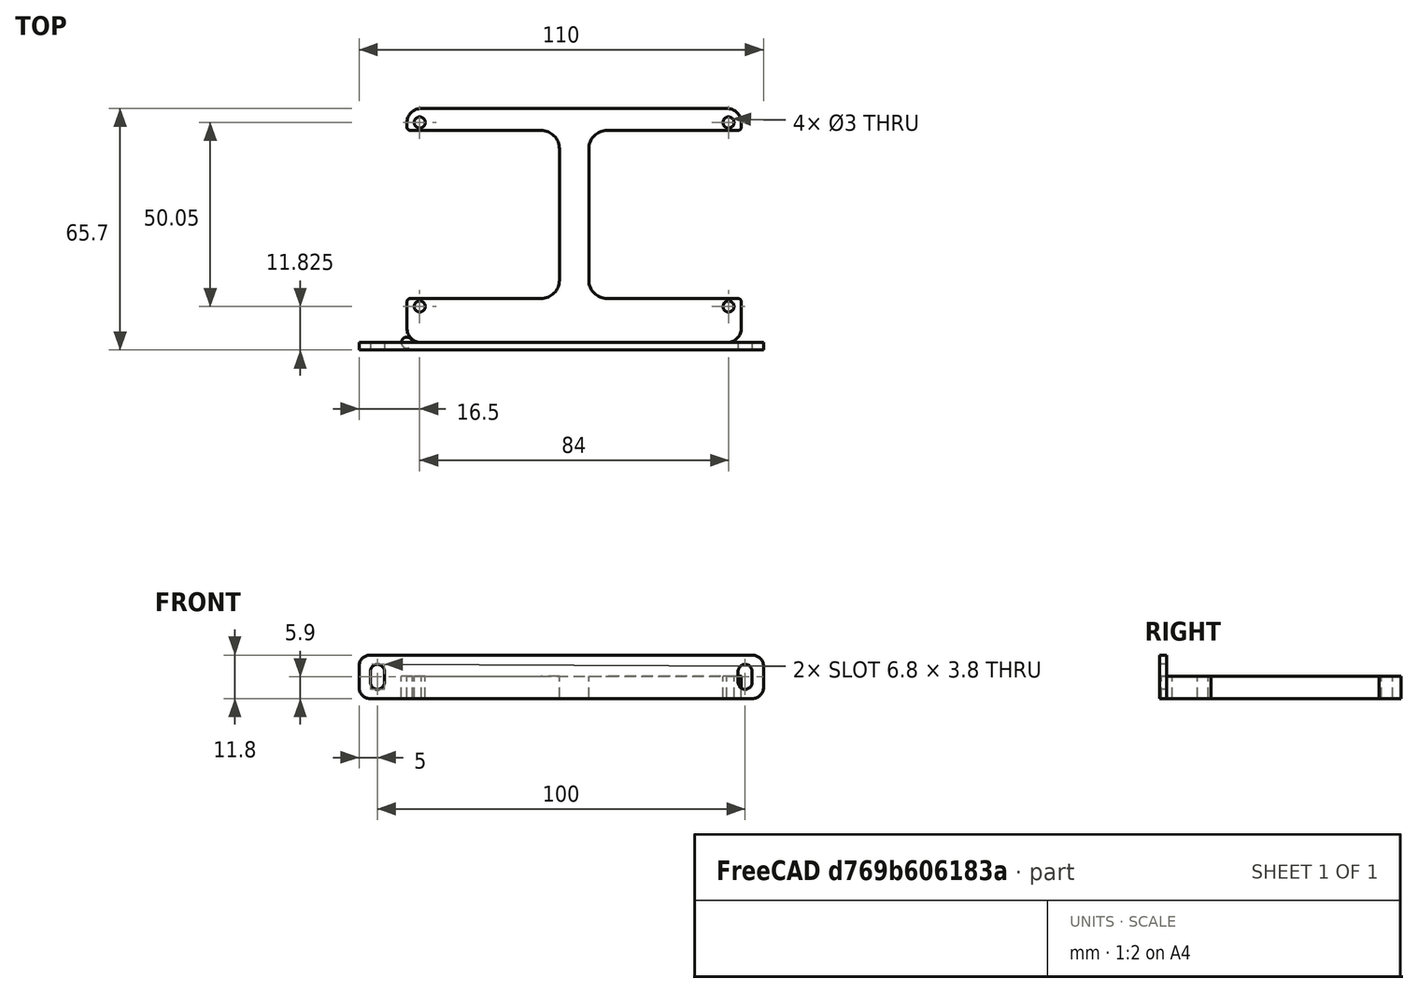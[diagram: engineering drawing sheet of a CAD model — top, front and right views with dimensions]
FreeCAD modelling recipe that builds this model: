
FCSTD DOCUMENT  (FreeCAD 0.19R23578 (Git))
Label: 3.2_320x240_lcd
License: All rights reserved
LicenseURL: http://en.wikipedia.org/wiki/All_rights_reserved
objects: Part::Fillet×3, Part::Box×2, Part::MultiFuse×2, Spreadsheet::Sheet×1, Part::Cylinder×1, Part::FeaturePython×1, Part::Feature×1, Part::Mirroring×1, Part::Cut×1
note: 11 computed .brp shape members not serialized (recipe doc carries the construction recipe); baked Part::Feature solids carry a one-line shape summary decoded from their .brp

FEATURE [Part::Box] Box  label="base cube"
  AttacherType = Attacher::AttachEngine3D
  Height = 6
  Length = 91
  Width = 63.7
  expr: Height = <<p>>.plate_z
  expr: Width = <<p>>.pcb_y + <<p>>.y_offset
  expr: Length = <<p>>.pcb_x
FEATURE [Spreadsheet::Sheet] Spreadsheet  label="p"
  cells = A1=hole_dist_x; B1(hole_dist_x)==84mm; A2=hole_dist_y; B2(hole_dist_y)==50.05mm; A3=hole_r; B3(hole_r)==1.5mm; A4=pcb_x; B4(pcb_x)==91mm; A5=pcb_y; B5(pcb_y)==57.7mm; A6=x_plate_y; B6(x_plate_y)==6mm; A7=y_plate_x; B7(y_plate_x)==8mm; A8=plate_z; B8(plate_z)==6mm; A9=y_offset; B9(y_offset)==6mm
FEATURE [Part::Fillet] Fillet  label="base cube fillet"
  Base = -> Box
  Edges = 4 edges r=4: [Edge1,Edge3,Edge5,Edge7]
FEATURE [Part::Box] Box001  label="base cube extract"
  AttacherType = Attacher::AttachEngine3D
  Height = 6
  Length = 41.5
  Placement = pos=(0,6,0) rot=(0,0,1;0rad)
  Width = 45.7
  expr: Length = (<<p>>.pcb_x - <<p>>.y_plate_x) / 2
  expr: .Placement.Base.y = <<p>>.x_plate_y
  expr: Width = <<p>>.pcb_y - <<p>>.x_plate_y * 2
  expr: Height = <<p>>.plate_z
FEATURE [Part::Cylinder] Cylinder  label="hole"
  Angle = 360
  AttacherType = Attacher::AttachEngine3D
  Height = 6
  Radius = 1.5
  expr: Height = <<p>>.plate_z
  expr: Radius = <<p>>.hole_r
FEATURE [Part::FeaturePython] Array  label="hole array"  # Draft array (typed FeaturePython)
  Angle = 360
  ArrayType = 0
  Axis = (0,0,1)
  Base = -> Cylinder
  Center = (0,0,0)
  Count = 4
  ExpandArray = false
  Fuse = false
  IntervalAxis = (0,0,0)
  IntervalX = (84,0,0)
  IntervalY = (0,50.05,0)
  IntervalZ = (0,0,100)
  NumberCircles = 3
  NumberPolar = 5
  NumberX = 2
  NumberY = 2
  NumberZ = 1
  Placement = pos=(3.5,3.825,0) rot=(0,0,1;0rad)
  PlacementList = 4 placements: [(0,0,0),(0,50.05,0),(84,0,0),(84,50.05,0)]
  RadialDistance = 50
  ScaleList = (4) [(1,1,1),(1,1,1),(1,1,1),(1,1,1)]
  Symmetry = 1
  TangentialDistance = 25
  expr: .Placement.Base.y = (<<p>>.pcb_y - <<p>>.hole_dist_y) / 2
  expr: .Placement.Base.x = (<<p>>.pcb_x - <<p>>.hole_dist_x) / 2
  expr: .IntervalY.y = <<p>>.hole_dist_y
  expr: .IntervalX.x = <<p>>.hole_dist_x
FEATURE [Part::Feature] Body002  label="attach plane x rotated dir001"
  Placement = pos=(-13,0,0) rot=(1,0,0;1.5708rad)
  shape: bbox 110 x 2 x 11.8 mm, 18 faces (baked)
FEATURE [Part::MultiFuse] Fusion001  label="body fusion"
  Shapes = -> [Fillet,Body002]
FEATURE [Part::Fillet] Fillet001  label="base cube extract fillet"
  Base = -> Box001
  Edges = 2 edges r=5: [Edge5,Edge7]
FEATURE [Part::Mirroring] Part__Mirroring  label="base cube extract (Mirror #1)"
  Base = (45.5,0,0)
  Normal = (1,0,0)
  Source = -> Fillet001
  expr: .Base.x = <<p>>.pcb_x / 2
FEATURE [Part::MultiFuse] Fusion  label="extract fusion"
  Placement = pos=(0,6,0) rot=(0,0,1;0rad)
  Shapes = -> [Part__Mirroring,Array,Fillet001]
  expr: .Placement.Base.y = <<p>>.y_offset
FEATURE [Part::Cut] Cut  label="body cut"
  Base = -> Fusion001
  Tool = -> Fusion
FEATURE [Part::Fillet] Fillet002  label="body fillet"
  Base = -> Cut
  Edges = 4 edges r=1: [Edge102,Edge103,Edge108,Edge113]
